ASSEMBLY  parts=2 mates=1
PART A: 120 faces, bbox 160.5x80.2x50.2 mm
  f0: plane 118x78mm, normal (0,0,1), area 9099.7mm2, adj f1,f97,f98,f99,f100,f101,f102,f103
  f1: cylinder r=1mm len=49mm, axis (0,0,1), area 77mm2, adj f0,f2,f97,f119
  f2: plane 120x80mm, normal (0,0,1), area 464.3mm2, adj f1,f3,f5,f6,f7,f8,f9,f87
  f3: cylinder r=3mm len=50mm, axis (0,0,-1), area 235.6mm2, adj f2,f4,f5,f88
  f4: plane 120x80mm, normal (0,0,-1), area 9592.3mm2, adj f3,f5,f6,f7,f8,f9,f87,f88
  f5: plane 74x50mm, normal (1,0,0), area 3700mm2, adj f2,f3,f4,f6
  f6: cylinder r=3mm len=50mm, axis (0,0,1), area 235.6mm2, adj f2,f4,f5,f7
  f7: plane 114x50mm, normal (0,-1,0), area 5700mm2, adj f2,f4,f6,f8
  f8: cylinder r=3mm len=50mm, axis (0,0,-1), area 235.6mm2, adj f2,f4,f7,f9
  f9: plane 74x50mm, normal (-1,0,0), area 3385.8mm2, adj f2,f4,f8,f10,f87
  f10: cylinder r=10mm len=39mm, axis (1,0,0), area 2450.4mm2, adj f9,f11
  f11: cone r=9mm half-angle=45deg, axis (1,0,0), area 84.4mm2, adj f10,f12
  f12: plane 18.22x18.22mm, normal (-1,0,0), area 44.6mm2, adj f11,f13,f84,f85,f86
  f13: cylinder r=8mm len=6.4mm, axis (1,0,0), area 0.3mm2, adj f12,f14,f84
  f14: cylinder r=8mm len=16mm, axis (1,0,0), area 4.3mm2, adj f13,f15,f84,f86
  f15: cylinder r=8mm len=16mm, axis (1,0,0), area 4.4mm2, adj f14,f16,f84,f86
  f16: cylinder r=8mm len=16mm, axis (1,0,0), area -40.1mm2, adj f15,f17,f84,f86
  f17: cylinder r=8mm len=16mm, axis (1,0,0), area 18mm2, adj f16,f18,f84,f86
  f18: cylinder r=8mm len=16mm, axis (1,0,0), area -39.6mm2, adj f17,f19,f84,f86
  f19: cylinder r=8mm len=16mm, axis (1,0,0), area 18mm2, adj f18,f20,f84,f86
  f20: cylinder r=8mm len=16mm, axis (1,0,0), area 18.9mm2, adj f19,f21,f84,f86
  f21: cylinder r=8mm len=16mm, axis (1,0,0), area 38.8mm2, adj f20,f22,f84,f86
  f22: cylinder r=8mm len=16mm, axis (1,0,0), area 4.3mm2, adj f21,f23,f84,f86
  f23: cylinder r=8mm len=16mm, axis (1,0,0), area 4.3mm2, adj f22,f24,f84,f86
  f24: cylinder r=8mm len=16mm, axis (1,0,0), area 4.3mm2, adj f23,f25,f84,f86
  f25: cylinder r=8mm len=16mm, axis (1,0,0), area 4.4mm2, adj f24,f26,f84,f86
  f26: cylinder r=8mm len=16mm, axis (1,0,0), area 4.3mm2, adj f25,f27,f84,f86
  f27: cylinder r=8mm len=16mm, axis (1,0,0), area 4.3mm2, adj f26,f28,f84,f86
  f28: cylinder r=8mm len=16mm, axis (1,0,0), area 4.4mm2, adj f27,f29,f84,f86
  f29: cylinder r=8mm len=16mm, axis (1,0,0), area 4.3mm2, adj f28,f30,f84,f86
  f30: cylinder r=8mm len=16mm, axis (1,0,0), area 4.2mm2, adj f29,f31,f84,f86
  f31: cylinder r=8mm len=16mm, axis (1,0,0), area -4.1mm2, adj f30,f32,f84,f86
  f32: cylinder r=8mm len=16mm, axis (1,0,0), area 142.7mm2, adj f31,f33,f84,f86
  f33: cylinder r=8mm len=16mm, axis (1,0,0), area 18mm2, adj f32,f34,f84,f86
  f34: cylinder r=8mm len=16mm, axis (1,0,0), area 4.3mm2, adj f33,f35,f84,f86
  f35: cylinder r=8mm len=16mm, axis (1,0,0), area 4.3mm2, adj f34,f36,f84,f86
  f36: cylinder r=8mm len=16mm, axis (1,0,0), area 4.3mm2, adj f35,f37,f84,f86
  f37: cylinder r=8mm len=16mm, axis (1,0,0), area -39.4mm2, adj f36,f38,f84,f86
  f38: cylinder r=8mm len=16mm, axis (1,0,0), area 17.9mm2, adj f37,f39,f84,f86
  f39: cylinder r=8mm len=16mm, axis (1,0,0), area 18.9mm2, adj f38,f40,f84,f86
  f40: cylinder r=8mm len=16mm, axis (1,0,0), area 38.7mm2, adj f39,f41,f84,f86
  f41: cylinder r=8mm len=16mm, axis (1,0,0), area 4.2mm2, adj f40,f42,f84,f86
  f42: cylinder r=8mm len=16mm, axis (1,0,0), area 4.2mm2, adj f41,f43,f84,f86
  f43: cylinder r=8mm len=16mm, axis (1,0,0), area 4.3mm2, adj f42,f44,f84,f86
  f44: cylinder r=8mm len=16mm, axis (1,0,0), area 4.4mm2, adj f43,f45,f84,f86
  f45: cylinder r=8mm len=16mm, axis (1,0,0), area 4.3mm2, adj f44,f46,f84,f86
  f46: cylinder r=8mm len=16mm, axis (1,0,0), area 4.3mm2, adj f45,f47,f84,f86
  f47: cylinder r=8mm len=16mm, axis (1,0,0), area 4.3mm2, adj f46,f48,f84,f86
  f48: cylinder r=8mm len=16mm, axis (1,0,0), area -40.1mm2, adj f47,f49,f84,f86
  f49: cylinder r=8mm len=16mm, axis (1,0,0), area 18mm2, adj f48,f50,f84,f86
  f50: cylinder r=8mm len=16mm, axis (1,0,0), area 4.2mm2, adj f49,f51,f84,f86
  f51: cylinder r=8mm len=16mm, axis (1,0,0), area 4.3mm2, adj f50,f52,f84,f86
  f52: cylinder r=8mm len=16mm, axis (1,0,0), area 4.3mm2, adj f51,f53,f84,f86
  f53: cylinder r=8mm len=16mm, axis (1,0,0), area 4.3mm2, adj f52,f54,f84,f86
  f54: cylinder r=8mm len=16mm, axis (1,0,0), area 3.2mm2, adj f53,f55,f84,f86
  f55: cylinder r=8mm len=16mm, axis (1,0,0), area 112.9mm2, adj f54,f56,f84,f86
  f56: cylinder r=8mm len=16mm, axis (1,0,0), area 17.9mm2, adj f55,f57,f84,f86
  f57: cylinder r=8mm len=16mm, axis (1,0,0), area 4.3mm2, adj f56,f58,f84,f86
  f58: cylinder r=8mm len=16mm, axis (1,0,0), area 4.3mm2, adj f57,f59,f84,f86
  f59: cylinder r=8mm len=16mm, axis (1,0,0), area -39.5mm2, adj f58,f60,f84,f86
  f60: cylinder r=8mm len=16mm, axis (1,0,0), area 17.9mm2, adj f59,f61,f84,f86
  f61: cylinder r=8mm len=16mm, axis (1,0,0), area 4.3mm2, adj f60,f62,f84,f86
  f62: cylinder r=8mm len=16mm, axis (1,0,0), area 4.3mm2, adj f61,f63,f84,f86
  f63: cylinder r=8mm len=16mm, axis (1,0,0), area 4.3mm2, adj f62,f64,f84,f86
  f64: cylinder r=8mm len=16mm, axis (1,0,0), area 18.9mm2, adj f63,f65,f84,f86
  f65: cylinder r=8mm len=16mm, axis (1,0,0), area 39mm2, adj f64,f66,f84,f86
  f66: cylinder r=8mm len=16mm, axis (1,0,0), area 4.3mm2, adj f65,f67,f84,f86
  f67: cylinder r=8mm len=16mm, axis (1,0,0), area 4.3mm2, adj f66,f68,f84,f86
  f68: cylinder r=8mm len=16mm, axis (1,0,0), area 4.2mm2, adj f67,f69,f84,f86
  f69: cylinder r=8mm len=16mm, axis (1,0,0), area 4.3mm2, adj f68,f70,f84,f86
  f70: cylinder r=8mm len=16mm, axis (1,0,0), area 4.4mm2, adj f69,f71,f84,f86
  f71: cylinder r=8mm len=16mm, axis (1,0,0), area 4.3mm2, adj f70,f72,f84,f86
  f72: cylinder r=8mm len=16mm, axis (1,0,0), area 4.3mm2, adj f71,f73,f84,f86
  f73: cylinder r=8mm len=16mm, axis (1,0,0), area 5.3mm2, adj f72,f74,f84,f86
  f74: cylinder r=8mm len=16mm, axis (1,0,0), area 4.3mm2, adj f73,f75,f84,f86
  f75: cylinder r=8mm len=16mm, axis (1,0,0), area 19mm2, adj f74,f76,f84,f86
  f76: cylinder r=8mm len=16mm, axis (1,0,0), area 3.2mm2, adj f75,f77,f84,f86
  f77: cylinder r=8mm len=16mm, axis (1,0,0), area 113.4mm2, adj f76,f78,f84,f86
  f78: cylinder r=8mm len=16mm, axis (1,0,0), area 17.9mm2, adj f77,f79,f84,f86
  f79: cylinder r=8mm len=16mm, axis (1,0,0), area 4.3mm2, adj f78,f80,f84,f86
  f80: cylinder r=8mm len=16mm, axis (1,0,0), area 4.2mm2, adj f79,f81,f84,f86
  f81: cylinder r=8mm len=16mm, axis (1,0,0), area 4.3mm2, adj f80,f82,f84,f86
  f82: cylinder r=8mm len=16mm, axis (1,0,0), area 25.3mm2, adj f81,f83,f84,f86,f113
  f83: plane 0.5x0.33mm, normal (0,0,-1), area 0.1mm2, adj f82,f84,f85,f86
  f84: bspline ~40.73x16.65mm, area 1364.3mm2, adj f12,f13,f14,f15,f16,f17,f18,f19
  f85: cylinder r=8.32mm len=40.67mm, axis (1,0,0), area -764.1mm2, adj f12,f83,f84,f86
  f86: bspline ~41.09x19.22mm, area 1339.5mm2, adj f12,f14,f15,f16,f17,f18,f19,f20
  f87: cylinder r=3mm len=50mm, axis (0,0,1), area 235.6mm2, adj f2,f4,f9,f88
  f88: plane 114x50mm, normal (0,1,0), area 5700mm2, adj f2,f3,f4,f87
  f89: cylinder r=1.5mm len=48mm, axis (0,0,1), area 452.4mm2, adj f2,f90
  f90: plane 3x3mm, normal (0,0,1), area 7.1mm2, adj f89
  f91: cylinder r=1.5mm len=48mm, axis (0,0,1), area 452.4mm2, adj f2,f92
  f92: plane 3x3mm, normal (0,0,1), area 7.1mm2, adj f91
  f93: cylinder r=1.5mm len=48mm, axis (0,0,1), area 452.4mm2, adj f2,f94
  f94: plane 3x3mm, normal (0,0,1), area 7.1mm2, adj f93
  f95: cylinder r=1.5mm len=48mm, axis (0,0,1), area 452.4mm2, adj f2,f96
  f96: plane 3x3mm, normal (0,0,1), area 7.1mm2, adj f95
  f97: plane 49x3mm, normal (-1,0,0), area 147mm2, adj f0,f1,f2,f98
  f98: cylinder r=1mm len=49mm, axis (0,0,1), area 77mm2, adj f0,f2,f97,f99
  f99: plane 49x3mm, normal (0,-1,0), area 147mm2, adj f0,f2,f98,f100
  f100: cylinder r=1mm len=49mm, axis (0,0,-1), area 77mm2, adj f0,f2,f99,f101
  f101: plane 64x49mm, normal (-1,0,0), area 3136mm2, adj f0,f2,f100,f102
  f102: cylinder r=3mm len=49mm, axis (0,0,-1), area 230.9mm2, adj f0,f2,f101,f103
  f103: plane 49x1mm, normal (0,1,0), area 49mm2, adj f0,f2,f102,f104
  f104: cylinder r=1mm len=49mm, axis (0,0,1), area 77mm2, adj f0,f2,f103,f105
  f105: plane 49x1mm, normal (-1,0,0), area 49mm2, adj f0,f2,f104,f106
  f106: cylinder r=3mm len=49mm, axis (0,0,-1), area 230.9mm2, adj f0,f2,f105,f107
  f107: plane 104x49mm, normal (0,1,0), area 5096mm2, adj f0,f2,f106,f108
  f108: cylinder r=1mm len=49mm, axis (0,0,1), area 77mm2, adj f0,f2,f107,f109
  f109: plane 49x3mm, normal (1,0,0), area 147mm2, adj f0,f2,f108,f110
  f110: cylinder r=1mm len=49mm, axis (0,0,1), area 77mm2, adj f0,f2,f109,f111
  f111: plane 49x3mm, normal (0,1,0), area 147mm2, adj f0,f2,f110,f112
  f112: cylinder r=1mm len=49mm, axis (0,0,-1), area 77mm2, adj f0,f2,f111,f113
  f113: plane 66x49mm, normal (1,0,0), area 3032.9mm2, adj f0,f2,f82,f112,f114
  f114: cylinder r=1mm len=49mm, axis (0,0,1), area 77mm2, adj f0,f2,f113,f115
  f115: plane 49x3mm, normal (0,-1,0), area 147mm2, adj f0,f2,f114,f116
  f116: cylinder r=1mm len=49mm, axis (0,0,1), area 77mm2, adj f0,f2,f115,f117
  f117: plane 49x3mm, normal (1,0,0), area 147mm2, adj f0,f2,f116,f118
  f118: cylinder r=1mm len=49mm, axis (0,0,1), area 77mm2, adj f0,f2,f117,f119
  f119: plane 106x49mm, normal (0,-1,0), area 5194mm2, adj f0,f1,f2,f118
PART B: 18 faces, bbox 120x80x2 mm
  f0: plane 114x2mm, normal (0,-1,0), area 228mm2, adj f8,f9,f14,f17
  f1: plane 74x2mm, normal (1,0,0), area 148mm2, adj f8,f9,f14,f15
  f2: plane 114x2mm, normal (0,1,0), area 228mm2, adj f8,f9,f15,f16
  f3: cylinder r=1.5mm len=3mm, axis (0,0,-1), area 9.4mm2, adj f9,f10
  f4: cylinder r=1.5mm len=3mm, axis (0,0,-1), area 9.4mm2, adj f9,f13
  f5: cylinder r=1.5mm len=3mm, axis (0,0,-1), area 9.4mm2, adj f9,f12
  f6: plane 74x2mm, normal (-1,0,0), area 148mm2, adj f8,f9,f16,f17
  f7: cylinder r=1.5mm len=3mm, axis (0,0,-1), area 9.4mm2, adj f9,f11
  f8: plane 120x80mm, normal (0,0,1), area 9513.7mm2, adj f0,f1,f2,f6,f10,f11,f12,f13
  f9: plane 120x80mm, normal (0,0,-1), area 9564mm2, adj f0,f1,f2,f3,f4,f5,f6,f7
  f10: cone r=1.5mm half-angle=45deg, axis (0,0,1), area 17.8mm2, adj f3,f8
  f11: cone r=1.5mm half-angle=45deg, axis (0,0,1), area 17.8mm2, adj f7,f8
  f12: cone r=1.5mm half-angle=45deg, axis (0,0,1), area 17.8mm2, adj f5,f8
  f13: cone r=1.5mm half-angle=45deg, axis (0,0,1), area 17.8mm2, adj f4,f8
  f14: cylinder r=3mm len=3mm, axis (0,0,1), area 9.4mm2, adj f0,f1,f8,f9
  f15: cylinder r=3mm len=3mm, axis (0,0,-1), area 9.4mm2, adj f1,f2,f8,f9
  f16: cylinder r=3mm len=3mm, axis (0,0,1), area 9.4mm2, adj f2,f6,f8,f9
  f17: cylinder r=3mm len=3mm, axis (0,0,-1), area 9.4mm2, adj f0,f6,f8,f9
PLACE A t=(6.99,-9.42,-106.66)mm fixed
PLACE B t=(6.99,-9.42,-57.66)mm
MATE slider B.f7 <-> A.f95  axis (0,0,-1) through (-49.51,-45.92,-56.66)mm
